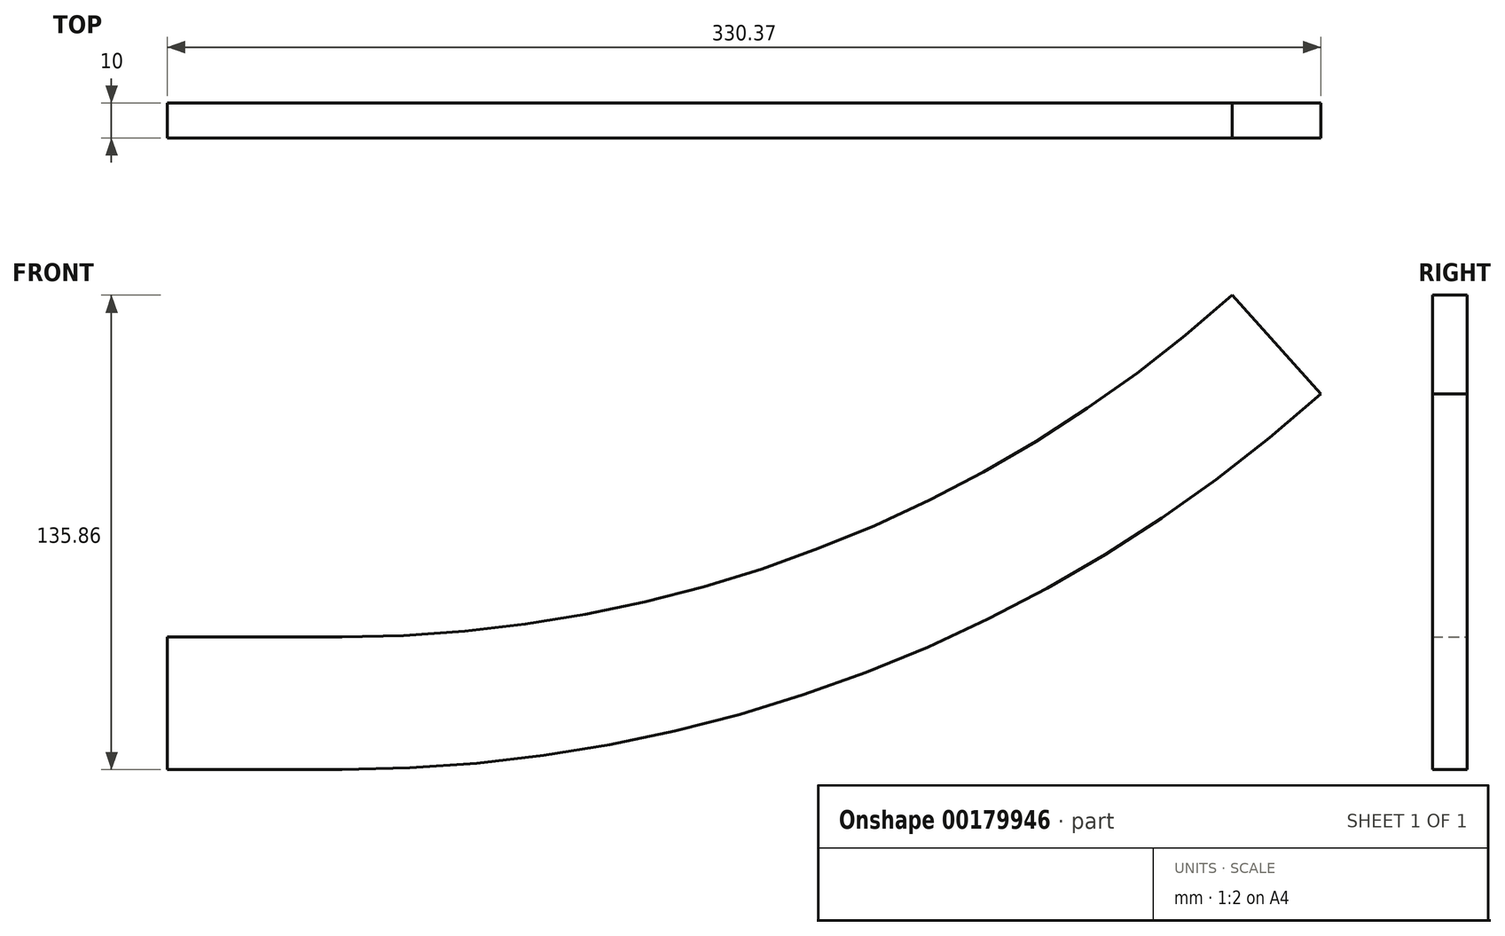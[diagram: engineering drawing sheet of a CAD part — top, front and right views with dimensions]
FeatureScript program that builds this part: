
annotation { "Feature Type Name" : "Feature", "Feature Type Description" : "" }
export const myFeature = defineFeature(function(context is Context, id is Id, definition is map)
    precondition{}
    {
        {
            var Q0;
            Q0=qCreatedBy(makeId("Front.planeOp"),FACE);
            var sketch = newSketch(context, id + "F0", { "sketchPlane" : qUnion([Q0])});
            skLineSegment(sketch, "E0.left", {"start": v(0, 0) * mm, "end": v(0, 400) * mm, "construction": true});
            skArc(sketch, "E1", {"start": v(0, 0) * mm, "mid": v(200, 53.59) * mm, "end": v(346.41, 200) * mm, "construction": true});
            skLineSegment(sketch, "E2", {"start": v(0, 400) * mm, "end": v(346.41, 200) * mm, "construction": true});
            skArc(sketch, "E3.0", {"start": v(0, -19) * mm, "mid": v(209.5, 37.14) * mm, "end": v(362.86, 190.5) * mm});
            skArc(sketch, "E4.0", {"start": v(0, 19) * mm, "mid": v(190.5, 70.04) * mm, "end": v(329.96, 209.5) * mm});
            skLineSegment(sketch, "E5", {"start": v(0, 400) * mm, "end": v(280.37, 88.62) * mm});
            skLineSegment(sketch, "E6", {"start": v(0, -19) * mm, "end": v(0, 19) * mm});
            skLineSegment(sketch, "E7", {"start": v(0, 19) * mm, "end": v(-50, 19) * mm});
            skLineSegment(sketch, "E8", {"start": v(-50, 19) * mm, "end": v(-50, -19) * mm});
            skLineSegment(sketch, "E9", {"start": v(-50, -19) * mm, "end": v(0, -19) * mm});
            skSolve(sketch);
        }
        {
            var Q0;
            Q0=qSketchRegion(id+"F0",true);
            extrude(context, id + "F1", {"entities" : qUnion([Q0]), "depth" : 10 * mm});
        }
    });
